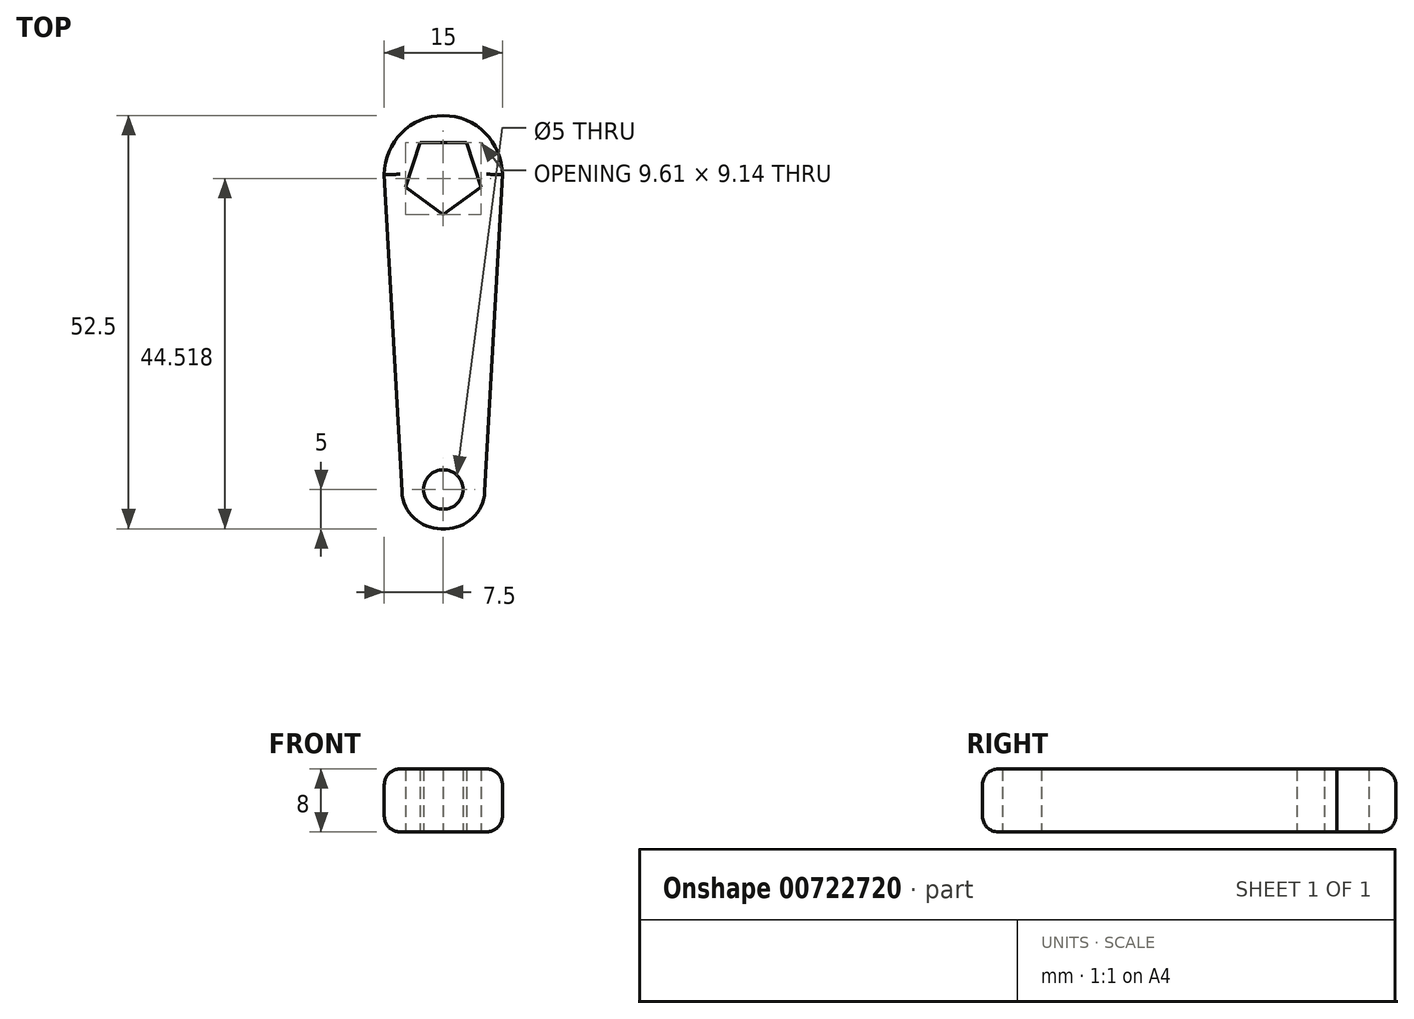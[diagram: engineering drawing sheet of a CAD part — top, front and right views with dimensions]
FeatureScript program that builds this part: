
annotation { "Feature Type Name" : "Feature", "Feature Type Description" : "" }
export const myFeature = defineFeature(function(context is Context, id is Id, definition is map)
    precondition{}
    {
        {
            var Q0;
            Q0=qCreatedBy(makeId("Top.planeOp"),FACE);
            var sketch = newSketch(context, id + "F0", { "sketchPlane" : qUnion([Q0])});
            skCircle(sketch, "E0.cCircle", {"center": v(0, 0) * mm, "radius": 5.05 * mm, "construction": true});
            skLineSegment(sketch, "E0.0", {"start": v(0, -5.05) * mm, "end": v(-4.8, -1.56) * mm});
            skLineSegment(sketch, "E0.1", {"start": v(-4.8, -1.56) * mm, "end": v(-2.97, 4.09) * mm});
            skLineSegment(sketch, "E0.2", {"start": v(-2.97, 4.09) * mm, "end": v(2.97, 4.09) * mm});
            skLineSegment(sketch, "E0.3", {"start": v(2.97, 4.09) * mm, "end": v(4.8, -1.56) * mm});
            skLineSegment(sketch, "E0.4", {"start": v(4.8, -1.56) * mm, "end": v(0, -5.05) * mm});
            skArc(sketch, "E1", {"start": v(7.5, 0) * mm, "mid": v(0, 7.5) * mm, "end": v(-7.5, 0) * mm});
            skLineSegment(sketch, "E2", {"start": v(0, 0) * mm, "end": v(0, -45) * mm, "construction": true});
            skLineSegment(sketch, "E3.bottom", {"start": v(-7.5, 0) * mm, "end": v(7.5, 0) * mm});
            skLineSegment(sketch, "E4", {"start": v(0, -45) * mm, "end": v(5, -45) * mm});
            skLineSegment(sketch, "E5", {"start": v(0, -45) * mm, "end": v(-5, -45) * mm});
            skLineSegment(sketch, "E6", {"start": v(-7.5, 0) * mm, "end": v(-5, -45) * mm});
            skLineSegment(sketch, "E7", {"start": v(7.5, 0) * mm, "end": v(5, -45) * mm});
            skLineSegment(sketch, "E8", {"start": v(0, -45) * mm, "end": v(0, -40) * mm, "construction": true});
            skCircle(sketch, "E9", {"center": v(0, -40) * mm, "radius": 2.5 * mm});
            skSolve(sketch);
        }
        {
            var Q0;
            Q0=qSketchRegion(id+"F0",true);
            extrude(context, id + "F1", {"entities" : qUnion([Q0]), "depth" : 8 * mm, "offsetDistance" : 25 * mm});
        }
        {
            var Q0;
            Q0=makeQuery(id+"F1.opExtrude","SWEPT_EDGE",EDGE,{"disambiguationData":[OSD([sQuery(id+"F0.wireOp",EDGE,"E5"),sQuery(id+"F0.wireOp",EDGE,"E6")])]});
            var Q1;
            Q1=makeQuery(id+"F1.opExtrude","SWEPT_EDGE",EDGE,{"disambiguationData":[OSD([sQuery(id+"F0.wireOp",EDGE,"E4"),sQuery(id+"F0.wireOp",EDGE,"E7")])]});
            fillet(context, id + "F2", {"entities" : qUnion([Q0, Q1]), "radius" : 5 * mm, "tangentPropagation" : true, "allowEdgeOverflow" : false});
        }
        {
            var Q0;
            Q0=makeQuery(id+"F1.opExtrude","CAP_EDGE",EDGE,{"disambiguationData":[OSD([sQuery(id+"F0.wireOp",EDGE,"E7")])],"isStart":false});
            var Q1;
            Q1=makeQuery(id+"F1.opExtrude","CAP_EDGE",EDGE,{"disambiguationData":[OSD([sQuery(id+"F0.wireOp",EDGE,"E1")])],"isStart":false});
            var Q2;
            Q2=makeQuery(id+"F1.opExtrude","CAP_EDGE",EDGE,{"disambiguationData":[OSD([sQuery(id+"F0.wireOp",EDGE,"E6")])],"isStart":true});
            var Q3;
            Q3=makeQuery(id+"F1.opExtrude","CAP_EDGE",EDGE,{"disambiguationData":[OSD([sQuery(id+"F0.wireOp",EDGE,"E1")])],"isStart":true});
            fillet(context, id + "F3", {"entities" : qUnion([Q0, Q1, Q2, Q3]), "radius" : 2 * mm, "tangentPropagation" : true, "allowEdgeOverflow" : false});
        }
    });
